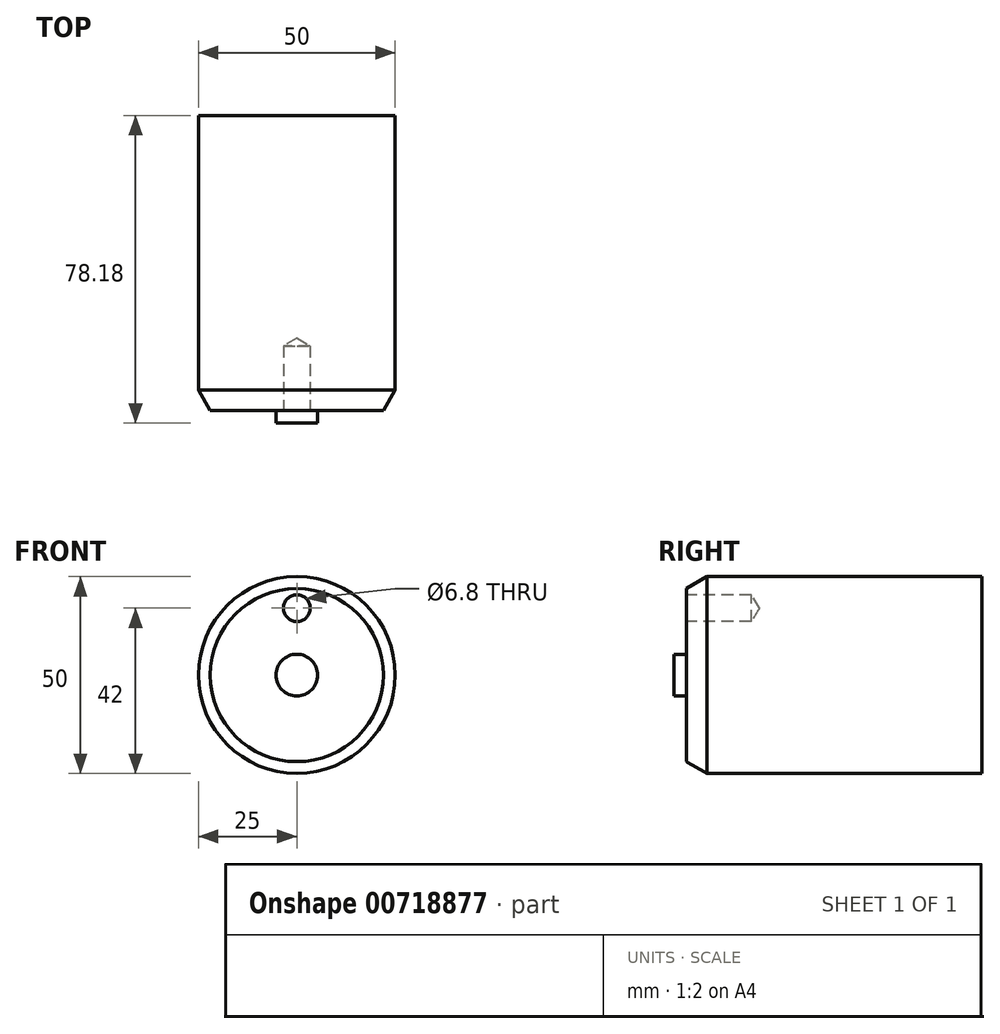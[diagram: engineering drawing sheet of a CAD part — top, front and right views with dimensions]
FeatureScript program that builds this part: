
annotation { "Feature Type Name" : "Feature", "Feature Type Description" : "" }
export const myFeature = defineFeature(function(context is Context, id is Id, definition is map)
    precondition{}
    {
        {
            var Q0;
            Q0=qCreatedBy(makeId("Front.planeOp"),FACE);
            var sketch = newSketch(context, id + "F0", { "sketchPlane" : qUnion([Q0])});
            skCircle(sketch, "E0", {"center": v(0, 0) * mm, "radius": 25 * mm});
            skSolve(sketch);
        }
        {
            var Q0;
            Q0=qSketchRegion(id+"F0",true);
            var Q1;
            Q1=sQuery(id+"F0.wireOp",EDGE,"E0");
            extrude(context, id + "F1", {"entities" : qUnion([Q0]), "surfaceEntities" : qUnion([Q1]), "oppositeDirection" : true, "depth" : 75 * mm, "offsetDistance" : 25.4 * mm});
        }
        {
            var Q0;
            Q0=makeQuery(id+"F1.opExtrude","CAP_FACE",FACE,{"disambiguationData":[OSD([sQuery(id+"F0.wireOp",EDGE,"E0")])],"isStart":true});
            var sketch = newSketch(context, id + "F2", { "sketchPlane" : qUnion([Q0])});
            skCircle(sketch, "E1", {"center": v(0, 0) * mm, "radius": 17 * mm, "construction": true});
            skLineSegment(sketch, "E2", {"start": v(0, 0) * mm, "end": v(0, 38.67) * mm, "construction": true});
            skPoint(sketch, "E3", {"position": v(0, 17) * mm});
            skSolve(sketch);
        }
        {
            var Q0;
            Q0=sQuery(id+"F2.wireOp",VERTEX,"E3");
            var Q1;
            Q1=makeQuery(id+"F1.opExtrude","SWEPT_BODY",BODY,{"disambiguationData":[OSD([sQuery(id+"F0.wireOp",EDGE,"E0")])]});
            hole(context, id + "F3", {"style" : HoleStyle.SIMPLE, "endStyle" : HoleEndStyle.BLIND, "standardTappedOrClearance" : lookupTablePath({ "standard" : "ISO", "engagement" : "75%", "pitch" : "1.25 mm", "size" : "M8", "type" : "Tapped" }), "standardBlindInLast" : lookupTablePath({ "standard" : "ISO", "engagement" : "75%", "pitch" : "1.25 mm", "size" : "M8", "type" : "Tapped" }), "holeDiameter" : 6.8 * mm, "majorDiameter" : 8 * mm, "showTappedDepth" : true, "holeDepth" : 16.45 * mm, "isTappedThrough" : true, "tappedDepth" : 12.7 * mm, "tapClearance" : 3, "locations" : qUnion([Q0]), "scope" : qUnion([Q1])});
        }
        {
            var Q0;
            Q0=makeQuery(id+"F1.opExtrude","CAP_FACE",FACE,{"disambiguationData":[OSD([sQuery(id+"F0.wireOp",EDGE,"E0")])],"isStart":true});
            var sketch = newSketch(context, id + "F4", { "sketchPlane" : qUnion([Q0])});
            skCircle(sketch, "E4", {"center": v(0, 0) * mm, "radius": 5.29 * mm});
            skSolve(sketch);
        }
        {
            var Q0;
            Q0=qSketchRegion(id+"F4",true);
            extrude(context, id + "F5", {"entities" : qUnion([Q0]), "operationType" : NewBodyOperationType.ADD, "depth" : 3.17 * mm, "offsetDistance" : 25.4 * mm});
        }
        {
            var Q0;
            Q0=makeQuery(id+"F1.opExtrude","CAP_EDGE",EDGE,{"disambiguationData":[OSD([sQuery(id+"F0.wireOp",EDGE,"E0")])],"isStart":true});
            chamfer(context, id + "F6", {"entities" : qUnion([Q0]), "chamferType" : ChamferType.OFFSET_ANGLE, "width" : 3 * mm, "oppositeDirection" : false, "angle" : 60 * degree, "tangentPropagation" : true});
        }
    });
